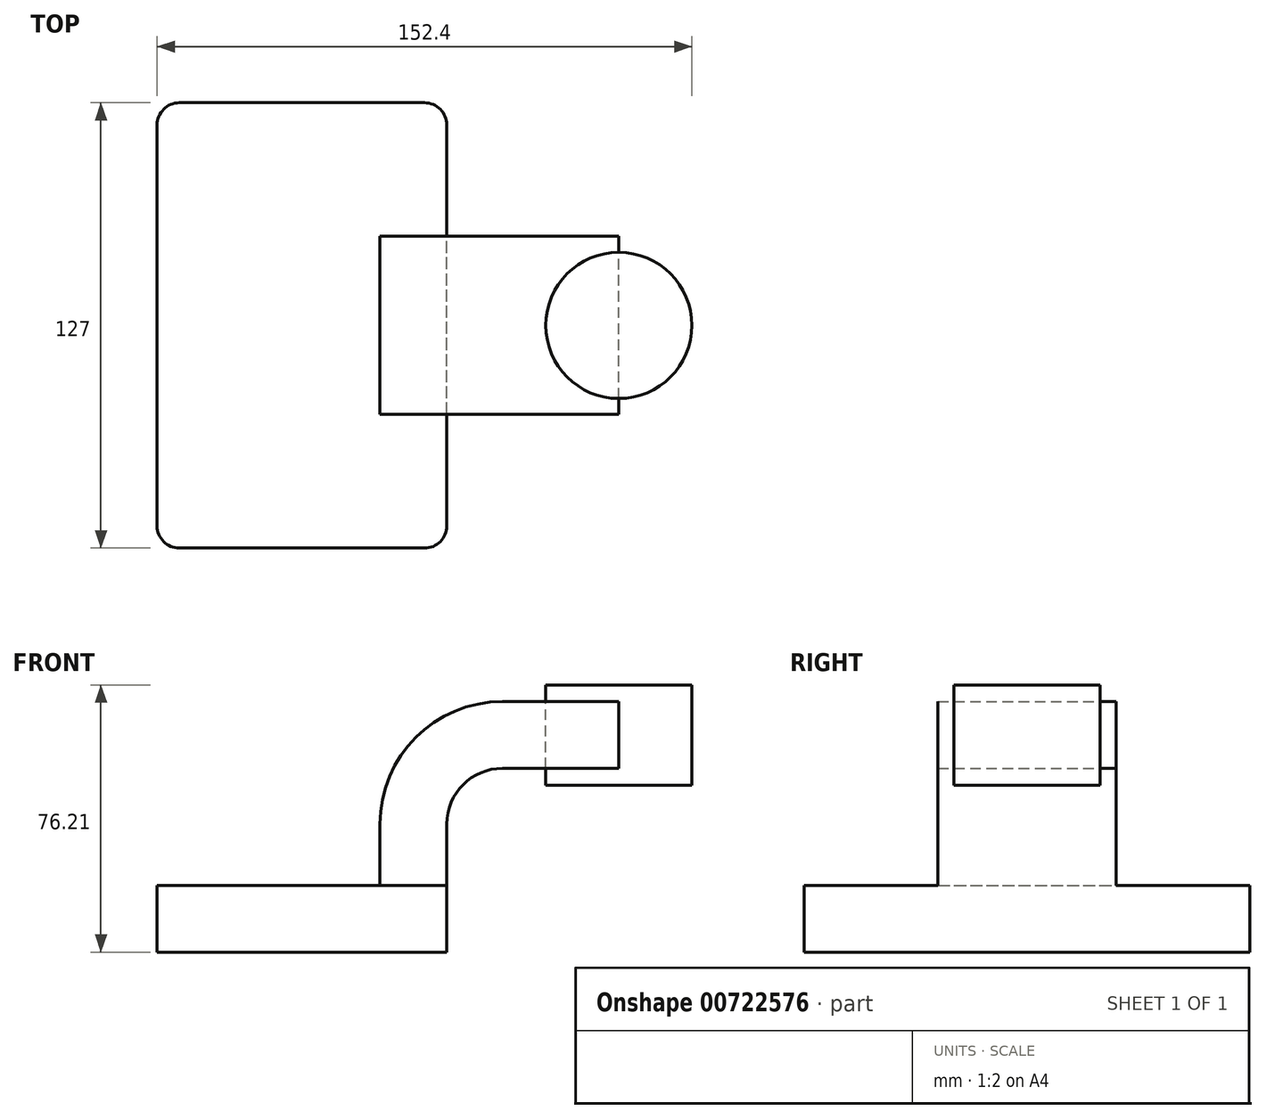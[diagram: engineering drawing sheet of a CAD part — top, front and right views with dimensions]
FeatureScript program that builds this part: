
annotation { "Feature Type Name" : "Feature", "Feature Type Description" : "" }
export const myFeature = defineFeature(function(context is Context, id is Id, definition is map)
    precondition{}
    {
        {
            var Q0;
            Q0=qCreatedBy(makeId("Front.planeOp"),FACE);
            var sketch = newSketch(context, id + "F0", { "sketchPlane" : qUnion([Q0])});
            skLineSegment(sketch, "E0.bottom", {"start": v(41.28, -9.52) * mm, "end": v(-41.28, -9.53) * mm});
            skLineSegment(sketch, "E0.top", {"start": v(41.28, 9.53) * mm, "end": v(-41.28, 9.52) * mm});
            skLineSegment(sketch, "E0.left", {"start": v(41.28, -9.52) * mm, "end": v(41.28, 9.53) * mm});
            skLineSegment(sketch, "E0.right", {"start": v(-41.28, -9.53) * mm, "end": v(-41.28, 9.52) * mm});
            skPoint(sketch, "E0.middle", {"position": v(0, 0) * mm});
            skLineSegment(sketch, "E1", {"start": v(41.28, 9.53) * mm, "end": v(41.28, 27) * mm});
            skArc(sketch, "E2", {"start": v(41.27, 27) * mm, "mid": v(45.92, 38.23) * mm, "end": v(57.15, 42.88) * mm});
            skLineSegment(sketch, "E3", {"start": v(57.15, 42.88) * mm, "end": v(90.3, 42.88) * mm});
            skLineSegment(sketch, "E4.bottom", {"start": v(111.12, 38.1) * mm, "end": v(60.32, 38.1) * mm});
            skLineSegment(sketch, "E4.top", {"start": v(111.12, 66.68) * mm, "end": v(60.32, 66.68) * mm});
            skLineSegment(sketch, "E4.left", {"start": v(111.12, 38.1) * mm, "end": v(111.12, 66.68) * mm});
            skLineSegment(sketch, "E4.right", {"start": v(60.32, 38.1) * mm, "end": v(60.32, 66.68) * mm});
            skPoint(sketch, "E4.middle", {"position": v(85.72, 52.39) * mm});
            skLineSegment(sketch, "E5.0", {"start": v(57.15, 61.93) * mm, "end": v(90.3, 61.93) * mm});
            skArc(sketch, "E5.1", {"start": v(22.23, 27) * mm, "mid": v(32.45, 51.7) * mm, "end": v(57.15, 61.93) * mm});
            skLineSegment(sketch, "E5.2", {"start": v(22.23, 9.53) * mm, "end": v(22.23, 27) * mm});
            skLineSegment(sketch, "E6", {"start": v(90.3, 42.88) * mm, "end": v(90.3, 61.93) * mm});
            skFitSpline(sketch, "E7", {"points": [v(-41.28, 9.53) * mm, v(57.15, 61.93) * mm], "startDerivative": vector(51.54, 85.58) * mm, "endDerivative": vector(121.1, -7.13) * mm});
            skLineSegment(sketch, "E8", {"start": v(90.3, 61.93) * mm, "end": v(90.3, 66.68) * mm});
            skLineSegment(sketch, "E9", {"start": v(90.3, 66.68) * mm, "end": v(90.3, 38.1) * mm});
            skSolve(sketch);
        }
        {
            var Q0;
            Q0=makeQuery(id+"F0.imprint","IMPRINT",FACE,{"disambiguationData":[TD([[makeQuery(id+"F0.imprint","IMPRINT",EDGE,{"derivedFrom":sQuery(id+"F0.wireOp",EDGE,"E0.bottom")}),-1.0]])]});
            extrude(context, id + "F1", {"entities" : qUnion([Q0]), "endBound" : BoundingType.SYMMETRIC, "depth" : 127 * mm, "offsetDistance" : 25.4 * mm});
        }
        {
            var Q0;
            {var subQ5=sQuery(id+"F0.wireOp",EDGE,"E1");Q0=makeQuery(id+"F0.imprint","IMPRINT",FACE,{"disambiguationData":[TD([[makeQuery(id+"F0.imprint","IMPRINT",EDGE,{"derivedFrom":subQ5}),1.0]])]});}
            var Q1;
            {var subQ0=sQuery(id+"F0.wireOp",EDGE,"E6");Q1=makeQuery(id+"F0.imprint","IMPRINT",FACE,{"disambiguationData":[TD([[makeQuery(id+"F0.imprint","IMPRINT",EDGE,{"derivedFrom":subQ0}),1.0]])]});}
            extrude(context, id + "F2", {"entities" : qUnion([Q0, Q1]), "operationType" : NewBodyOperationType.ADD, "endBound" : BoundingType.SYMMETRIC, "depth" : 50.8 * mm, "offsetDistance" : 25.4 * mm});
        }
        {
            var Q0;
            Q0=makeQuery(id+"F0.imprint","IMPRINT",FACE,{"disambiguationData":[TD([[makeQuery(id+"F0.imprint","IMPRINT",EDGE,{"derivedFrom":sQuery(id+"F0.wireOp",EDGE,"E5.1")}),1.0]])]});
            extrude(context, id + "F3", {"entities" : qUnion([Q0]), "operationType" : NewBodyOperationType.ADD, "endBound" : BoundingType.SYMMETRIC, "depth" : 15.88 * mm, "offsetDistance" : 25.4 * mm});
        }
        {
            var Q0;
            {var subQ0=sQuery(id+"F0.wireOp",EDGE,"E9");var subQ1=sQuery(id+"F0.wireOp",EDGE,"E3");var subQ2=makeQuery(id+"F0.imprint","INTERSECT",VERTEX,{"derivedFrom":[subQ1,subQ0]});Q0=makeQuery(id+"F0.imprint","IMPRINT",FACE,{"disambiguationData":[TD([[makeQuery(id+"F0.imprint","IMPRINT",EDGE,{"disambiguationData":[TD([[subQ2,1.0]])],"derivedFrom":subQ1}),1.0]])]});}
            extrude(context, id + "F4", {"entities" : qUnion([Q0]), "operationType" : NewBodyOperationType.ADD, "endBound" : BoundingType.SYMMETRIC, "depth" : 50.8 * mm, "offsetDistance" : 25.4 * mm});
        }
        {
            var Q0;
            {var subQ4=sQuery(id+"F0.wireOp",EDGE,"E4.left");Q0=makeQuery(id+"F0.imprint","IMPRINT",FACE,{"disambiguationData":[TD([[makeQuery(id+"F0.imprint","IMPRINT",EDGE,{"derivedFrom":subQ4}),1.0]])]});}
            var Q1;
            Q1=sQuery(id+"F0.wireOp",EDGE,"E9");
            revolve(context, id + "F5", {"surfaceOperationType" : NewSurfaceOperationType.NEW, "entities" : qUnion([Q0]), "axis" : qUnion([Q1]), "revolveType" : RevolveType.FULL});
        }
        {
            var Q0;
            Q0=makeQuery(id+"F1.opExtrude","CAP_EDGE",EDGE,{"disambiguationData":[OSD([sQuery(id+"F0.wireOp",EDGE,"E0.left")])],"isStart":false});
            var Q1;
            Q1=makeQuery(id+"F1.opExtrude","CAP_EDGE",EDGE,{"disambiguationData":[OSD([sQuery(id+"F0.wireOp",EDGE,"E0.right")])],"isStart":false});
            var Q2;
            Q2=makeQuery(id+"F1.opExtrude","CAP_EDGE",EDGE,{"disambiguationData":[OSD([sQuery(id+"F0.wireOp",EDGE,"E0.left")])],"isStart":true});
            var Q3;
            Q3=makeQuery(id+"F1.opExtrude","CAP_EDGE",EDGE,{"disambiguationData":[OSD([sQuery(id+"F0.wireOp",EDGE,"E0.right")])],"isStart":true});
            fillet(context, id + "F6", {"entities" : qUnion([Q0, Q1, Q2, Q3]), "radius" : 6.35 * mm, "tangentPropagation" : true, "allowEdgeOverflow" : false});
        }
    });
